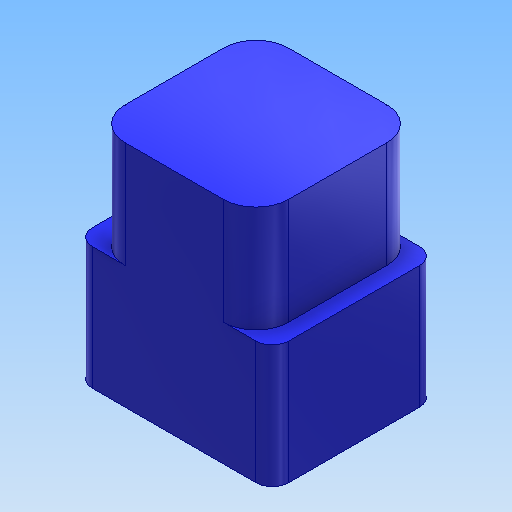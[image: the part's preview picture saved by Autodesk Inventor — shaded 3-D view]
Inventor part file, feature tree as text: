
AUTODESK INVENTOR PART (.ipt)
format: ipt  version: 2018 (Build 220112000, 112)  size: 145,408 bytes
history: native  units: mm
features: extrude x2, fillet x2, sketch x2
ambient origin geometry x8: Origin, YZ Plane, XZ Plane, XY Plane, X Axis, Y Axis, Z Axis, Center Point
bodies: Volumenkörper1 (feature_tree)
feature tree (6):
  extrude  "Extrusion1"  Depth=10.0mm
  extrude  "Extrusion2"  Depth=10.0mm
  fillet  "Rundung1"  Radius=10.0mm
  fillet  "Rundung2"  Radius=6.5mm
  sketch  "Skizze1"  dims[d0=12.0mm d1=10.0mm]
  sketch  "Skizze2"  dims[d2=14.0mm d3=0.0mm d4=10.0mm d5=10.0mm d6=6.5mm d7=0.0mm d8=2.0mm d9=1.0mm]
